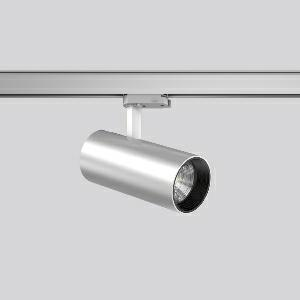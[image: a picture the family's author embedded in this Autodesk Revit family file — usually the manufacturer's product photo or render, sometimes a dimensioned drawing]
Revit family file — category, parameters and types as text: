
# Revit family: deecos_s_mini_742201_004_3_76_b498
name_source: partatom
category: Lighting Fixtures
units: mm (PartAtom-declared; Revit-internal decimal feet)

## family parameters
Cut with Voids When Loaded = No
Host = Face
Light Source = No
Part Type = Normal
Room Calculation Point = No
Round Connector Dimension = Use Diameter
Shared = No

## types (1)
- DEECOS S mini (1 x LED Modul 935, 2300 lm, 3500)
    Apparent Load = 20 VA
    Approval mark = CE
    CIE Flux Codes = 80 99 100 100 100
    Color Rendering = 92
    Color Temperature = 3500
    Default Elevation = 1800 mm
    Description = Series: DEECOS S mini
LED surface-mounted projector in modern design with no visible cooling ribs. Housing: die-cast aluminium, powder-coated. Rotation range: 356°. Swivel range: 90°. Black plastic ring and recessed LED to prevent glare from the side. Optical assembly with lens made of plastic (polycarbonate) for the best homogeneous light distribution - can be changed without tools. Best colour rendering index Ra>90. With adapter for RZB 3-circuit DALI tracks. Suitable for Track on ceiling, Wall track. High quality converter without flickering and stroboscopic effect. The following accessories can be mounted without use of tools: interchangeable lenses, decorative glasses, honeycomb louvre, clear and frosted diffusers, white interchangeable plastic ring. 
Colour: silver
Diameter: 87 mm
Height: 214 mm
Lamp: LED
Socket: without socket
Colour temperature: 3500K
Colour rendering index (CRI): 92
System power: 20 W
Rated luminous flux: 2300 lm
Luminous efficiency: 115 lm/W
Control gear: Converter, dimmable, DALI
Protection class: I
Type of protection: IP 20
    Height = 214 mm
    Lamp = 1 x LED Modul 935
    Lamp Light Flux = 2300 lm
    Lamp count = 1
    Length = 87 mm
    Lifetime = 50000 h
    Luminous efficacy = 115 lm/W
    Manufacturer = RZB
    ModVariant = No
    Model = 742201.004.3.76
    Mounting Place = Ceiling
    Mounting Type = Rail mounted
    Number of Poles = 1
    OnlyDefault = Yes
    Power Factor = 1
    Product Name = DEECOS S mini
    Product group = Track mounted projectors
    ProductGroupID = 301
    Protection Class = Protection class I
    Protection Degree = IP 20
    RLX_Detail_Level = 1
    RLX_Emergency_Light_Flux = 0 lm
    RLX_Emergency_Type = 0
    RLX_Emergency_Type_DB = No
    RlxData = <blob elided: 37593 chars, md5=dccd65e3>
    Socket = socket
    Standby Power = 0 W
    System Light Flux = 2300 lm
    System Power = 20 W
    Type Comments = Product without accessories
    Type Image = 741930.004.jpg
    URL = http://relux.com
    VarID = ---
    Voltage = 230 V
    Voltage Range = 220-240 V
    Weight = 0.00 kg
    Width = 0 mm  [stored 0 ft]

note: [stored X ft] marks values corroborated as IEEE doubles in the binary element streams (Revit-internal decimal feet)

## geometry (parser evidence)
native form markers: Blend x4, Sweep x12
no freeform markers — native parametric forms only
